# Revit family: 2CKA006800A2515
name_source: partatom
category: Elektroinstallationen
revit_build: Autodesk Revit 2017 (Build: 20160225_1515(x64)
units: mm (PartAtom-declared; Revit-internal decimal feet)

## family parameters
Basisbauteil = Fläche
Beim Laden mit Abzugskörper schneiden = Nein
Bemaßung runder Anschluss = Durchmesser verwenden
Beschriftungsausrichtung beibehalten = Nein
Gemeinsam genutzt = Nein
Raumberechnungspunkt = Nein
Teiletyp = Normal

## types (1)
- 2CKA006800A2515
    Art des Zubehörs = Relaismodul
    BIM = https://media.live.bim.site
    BIMSITE_PRODUCT_ID = e76546f078a542a7099147b105aa35ce833bee2d
    Beschreibung = Busch-Rauchalarm Relais, studioweiß, Sicherheitstechnik, Busch-Rauchalarm ProfessionalLINE, Busch-Rauchalarm Relais Geeignet für die Anbindung an externe Systeme wie z.B. KNX über entsprechende Binäreingänge. Geeignet für die Anbindung an externe Systeme wie z. B. Busch-free@home über entsprechende Binäreingänge oder Nebenstelleneingänge der Wireless Sensor-/Aktor-Kombinationen (z.B.6211/1.1-WL). Relaiskontakt: potentialfreier Wechsler 230 V~ max. 5A Leitungsanschluss: bis zu 2 x 2 x 1,5 mm² Mit eingebautem Funkmodul.
    Datenblatt = https://media.live.bim.site
    GTIN = 4011395137468
    Gerätebreite [mm] = 141
    Gerätehöhe [mm] = 29
    Gerätetiefe [mm] = 141
    Gewicht [kg/m] = 0.26
    HAN = 2CKA006800A2515
    HeinzeBIM = https://www.heinze.de
    Hersteller = Busch-Jaeger
    Ist System = Nein
    Ist Zubehör = Nein
    Produktseite = https://media.live.bim.site
    TYPE = 6829-84
    Typname = Busch-Rauchalarm Relais, studioweiß, Sicherheitstechnik, Busch-Rauchalarm ProfessionalLINE
    URL = https://www.busch-jaeger.de
    Vorgabe-Ansicht = 1219 mm

## geometry (parser evidence)
native form markers: Sweep x2
no freeform markers — native parametric forms only
